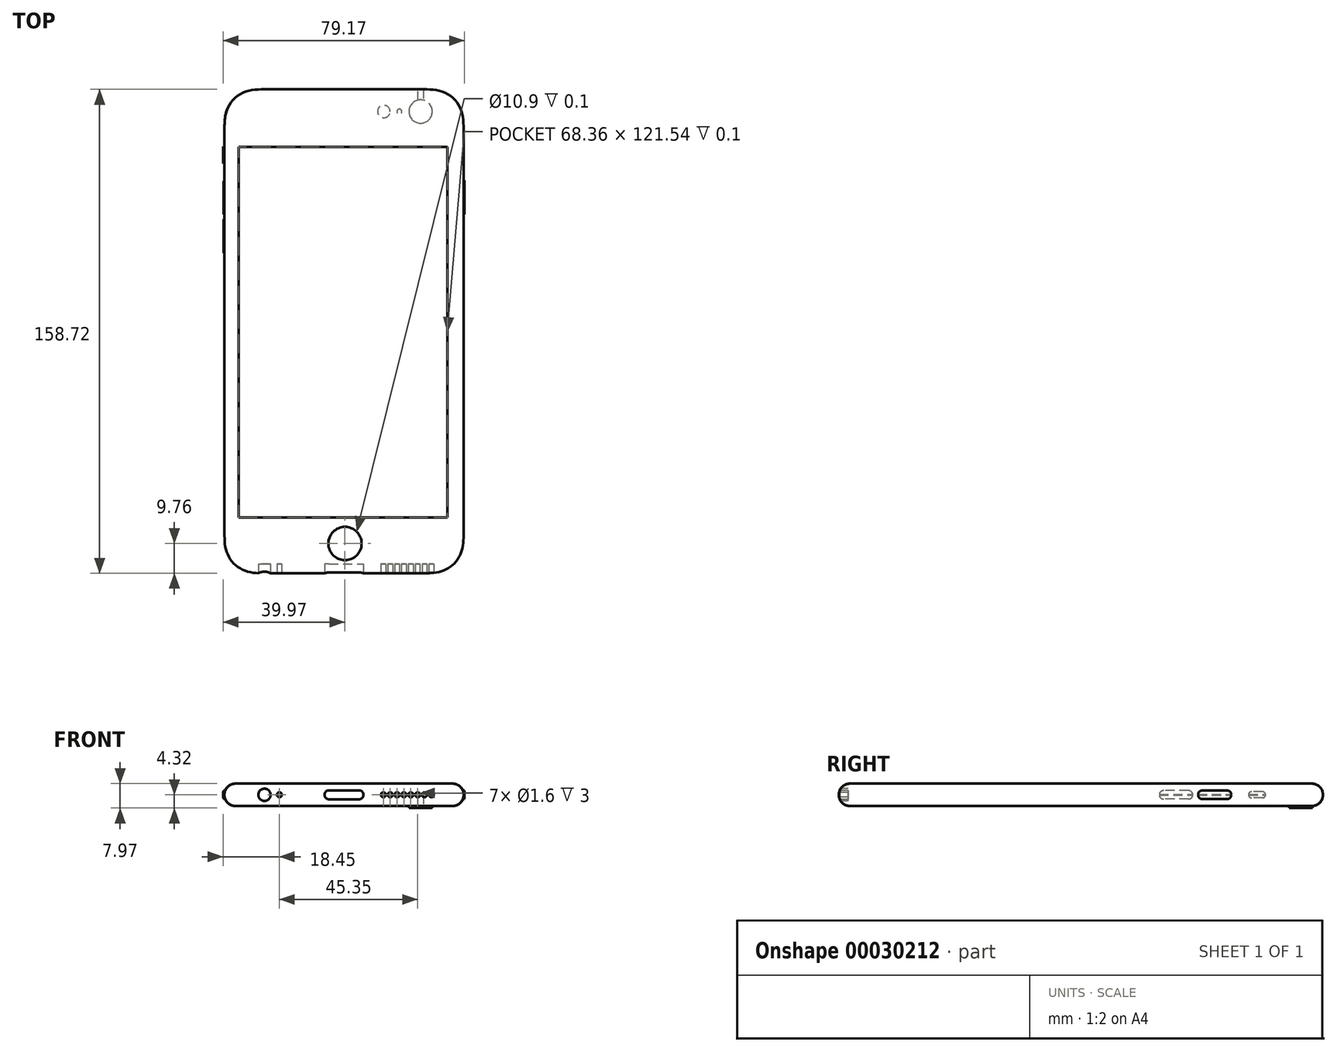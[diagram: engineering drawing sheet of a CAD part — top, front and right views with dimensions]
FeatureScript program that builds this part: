
annotation { "Feature Type Name" : "Feature", "Feature Type Description" : "" }
export const myFeature = defineFeature(function(context is Context, id is Id, definition is map)
    precondition{}
    {
        {
            var Q0;
            Q0=qCreatedBy(makeId("Top.planeOp"),FACE);
            var sketch = newSketch(context, id + "F0", { "sketchPlane" : qUnion([Q0])});
            skLineSegment(sketch, "E0.rect.bottom", {"start": v(25.09, -79.36) * mm, "end": v(-25.09, -79.36) * mm});
            skLineSegment(sketch, "E0.rect.top", {"start": v(25.09, 79.36) * mm, "end": v(-25.09, 79.36) * mm});
            skLineSegment(sketch, "E0.rect.left", {"start": v(39.22, -65.23) * mm, "end": v(39.22, 65.23) * mm});
            skLineSegment(sketch, "E0.rect.right", {"start": v(-39.22, -65.23) * mm, "end": v(-39.22, 65.23) * mm});
            skPoint(sketch, "E0.rect.middle", {"position": v(0, 0) * mm});
            skCircle(sketch, "E1", {"center": v(25.12, 72.09) * mm, "radius": 3.83 * mm});
            skCircle(sketch, "E2", {"center": v(18.16, 72.09) * mm, "radius": 0.8 * mm});
            skCircle(sketch, "E3", {"center": v(13.06, 72.09) * mm, "radius": 2.06 * mm});
            skLineSegment(sketch, "E4", {"start": v(-39.22, 72.1) * mm, "end": v(39.22, 72.1) * mm, "construction": true});
            skPoint(sketch, "E5.visualSharp", {"position": v(-39.22, 79.36) * mm});
            skFitSpline(sketch, "E6", {"points": [v(-25.09, 79.36) * mm, v(-29.02, 79.25) * mm, v(-32.83, 78.38) * mm, v(-36.09, 76.23) * mm, v(-38.24, 72.97) * mm, v(-39.1, 69.16) * mm, v(-39.22, 65.23) * mm], "startDerivative": vector(-8.98, 0) * mm, "endDerivative": vector(0, -8.98) * mm});
            skLineSegment(sketch, "E7", {"start": v(-25.09, 79.36) * mm, "end": v(-39.22, 79.36) * mm, "construction": true});
            skLineSegment(sketch, "E8", {"start": v(-39.22, 79.36) * mm, "end": v(-39.22, 65.23) * mm, "construction": true});
            skLineSegment(sketch, "E9", {"start": v(0, 79.36) * mm, "end": v(0, -79.36) * mm, "construction": true});
            skLineSegment(sketch, "E10", {"start": v(-39.22, 0) * mm, "end": v(39.22, 0) * mm, "construction": true});
            skFitSpline(sketch, "E11.MirrorCS", {"points": [v(25.09, 79.36) * mm, v(29.02, 79.25) * mm, v(32.83, 78.38) * mm, v(36.09, 76.23) * mm, v(38.24, 72.97) * mm, v(39.1, 69.16) * mm, v(39.22, 65.23) * mm], "startDerivative": vector(8.98, 0) * mm, "endDerivative": vector(0, -8.98) * mm});
            skFitSpline(sketch, "E12.MirrorCS", {"points": [v(-25.09, -79.36) * mm, v(-29.02, -79.25) * mm, v(-32.83, -78.38) * mm, v(-36.09, -76.23) * mm, v(-38.24, -72.97) * mm, v(-39.1, -69.16) * mm, v(-39.22, -65.23) * mm], "startDerivative": vector(-8.98, 0) * mm, "endDerivative": vector(0, 8.98) * mm});
            skFitSpline(sketch, "E13.MirrorCS", {"points": [v(25.09, -79.36) * mm, v(29.02, -79.25) * mm, v(32.83, -78.38) * mm, v(36.09, -76.23) * mm, v(38.24, -72.97) * mm, v(39.1, -69.16) * mm, v(39.22, -65.23) * mm], "startDerivative": vector(8.98, 0) * mm, "endDerivative": vector(0, 8.98) * mm});
            skCircle(sketch, "E14", {"center": v(0, 37.36) * mm, "radius": 11 * mm, "construction": true});
            skSolve(sketch);
        }
        {
            var Q0;
            Q0=makeQuery(id+"F0.imprint","IMPRINT",FACE,{"disambiguationData":[TD([[makeQuery(id+"F0.imprint","IMPRINT",EDGE,{"derivedFrom":sQuery(id+"F0.wireOp",EDGE,"E0.rect.bottom")}),-1.0]])]});
            var Q1;
            Q1=makeQuery(id+"F0.imprint","IMPRINT",FACE,{"disambiguationData":[TD([[makeQuery(id+"F0.imprint","IMPRINT",EDGE,{"derivedFrom":sQuery(id+"F0.wireOp",EDGE,"E1")}),1.0]])]});
            var Q2;
            Q2=makeQuery(id+"F0.imprint","IMPRINT",FACE,{"disambiguationData":[TD([[makeQuery(id+"F0.imprint","IMPRINT",EDGE,{"derivedFrom":sQuery(id+"F0.wireOp",EDGE,"E2")}),1.0]])]});
            var Q3;
            Q3=makeQuery(id+"F0.imprint","IMPRINT",FACE,{"disambiguationData":[TD([[makeQuery(id+"F0.imprint","IMPRINT",EDGE,{"derivedFrom":sQuery(id+"F0.wireOp",EDGE,"E3")}),1.0]])]});
            extrude(context, id + "F1", {"entities" : qUnion([Q0, Q1, Q2, Q3]), "depth" : 7.3 * mm});
        }
        {
            var Q0;
            Q0=makeQuery(id+"F0.imprint","IMPRINT",FACE,{"disambiguationData":[TD([[makeQuery(id+"F0.imprint","IMPRINT",EDGE,{"derivedFrom":sQuery(id+"F0.wireOp",EDGE,"E1")}),1.0]])]});
            extrude(context, id + "F2", {"entities" : qUnion([Q0]), "operationType" : NewBodyOperationType.ADD, "oppositeDirection" : true, "depth" : 0.67 * mm});
        }
        {
            var Q0;
            Q0=makeQuery(id+"F0.imprint","IMPRINT",FACE,{"disambiguationData":[TD([[makeQuery(id+"F0.imprint","IMPRINT",EDGE,{"derivedFrom":sQuery(id+"F0.wireOp",EDGE,"E3")}),1.0]])]});
            var Q1;
            Q1=makeQuery(id+"F0.imprint","IMPRINT",FACE,{"disambiguationData":[TD([[makeQuery(id+"F0.imprint","IMPRINT",EDGE,{"derivedFrom":sQuery(id+"F0.wireOp",EDGE,"E2")}),1.0]])]});
            extrude(context, id + "F3", {"entities" : qUnion([Q0, Q1]), "operationType" : NewBodyOperationType.REMOVE, "depth" : 0.1 * mm});
        }
        {
            var Q0;
            Q0=makeQuery(id+"F1.opExtrude","CAP_FACE",FACE,{"disambiguationData":[OSD([sQuery(id+"F0.wireOp",EDGE,"E0.rect.bottom"),sQuery(id+"F0.wireOp",EDGE,"E0.rect.top"),sQuery(id+"F0.wireOp",EDGE,"E0.rect.left"),sQuery(id+"F0.wireOp",EDGE,"E0.rect.right"),sQuery(id+"F0.wireOp",EDGE,"d7852d5b-fe0f-4a90-bdf2-04cff158e1f8.filletArc"),sQuery(id+"F0.wireOp",EDGE,"E5.filletArc"),sQuery(id+"F0.wireOp",EDGE,"7c06d2e9-cdf6-4879-9dee-aab3bc7c6033.filletArc"),sQuery(id+"F0.wireOp",EDGE,"93b3bdb9-dbb8-49f8-8f1e-002f612095da.filletArc")])],"isStart":false});
            var sketch = newSketch(context, id + "F4", { "sketchPlane" : qUnion([Q0])});
            skCircle(sketch, "E15", {"center": v(0.32, -69.6) * mm, "radius": 5.45 * mm});
            skLineSegment(sketch, "E16.bottom", {"start": v(-34.51, 60.44) * mm, "end": v(33.85, 60.44) * mm});
            skLineSegment(sketch, "E16.top", {"start": v(-34.5, -61.1) * mm, "end": v(33.85, -61.1) * mm});
            skLineSegment(sketch, "E16.left", {"start": v(-34.51, 60.44) * mm, "end": v(-34.5, -61.1) * mm});
            skLineSegment(sketch, "E16.right", {"start": v(33.85, 60.44) * mm, "end": v(33.85, -61.1) * mm});
            skSolve(sketch);
        }
        {
            var Q0;
            Q0=makeQuery(id+"F4.imprint","IMPRINT",FACE,{"disambiguationData":[TD([[makeQuery(id+"F4.imprint","IMPRINT",EDGE,{"derivedFrom":sQuery(id+"F4.wireOp",EDGE,"E15")}),1.0]])]});
            extrude(context, id + "F5", {"entities" : qUnion([Q0]), "operationType" : NewBodyOperationType.REMOVE, "oppositeDirection" : true, "depth" : 0.1 * mm});
        }
        {
            var Q0;
            Q0=makeQuery(id+"F4.imprint","IMPRINT",FACE,{"disambiguationData":[TD([[makeQuery(id+"F4.imprint","IMPRINT",EDGE,{"derivedFrom":sQuery(id+"F4.wireOp",EDGE,"E16.bottom")}),-1.0]])]});
            extrude(context, id + "F6", {"entities" : qUnion([Q0]), "operationType" : NewBodyOperationType.REMOVE, "oppositeDirection" : true, "depth" : 0.1 * mm});
        }
        {
            var Q0;
            Q0=makeQuery(id+"F1.opExtrude","SWEPT_FACE",FACE,{"disambiguationData":[OSD([sQuery(id+"F0.wireOp",EDGE,"E0.rect.bottom")])]});
            var sketch = newSketch(context, id + "F7", { "sketchPlane" : qUnion([Q0])});
            skLineSegment(sketch, "E17.0", {"start": v(25.09, 7.3) * mm, "end": v(-25.09, 7.3) * mm, "construction": true});
            skLineSegment(sketch, "E17.1", {"start": v(25.09, 0) * mm, "end": v(-25.09, 0) * mm, "construction": true});
            skLineSegment(sketch, "E17.2", {"start": v(39.22, 7.3) * mm, "end": v(39.22, 0) * mm, "construction": true});
            skLineSegment(sketch, "E17.3", {"start": v(-39.22, 7.3) * mm, "end": v(-39.22, 0) * mm, "construction": true});
            skFitSpline(sketch, "E17.4", {"points": [v(-24.74, 7.3) * mm, v(-29.45, 7.3) * mm, v(-34.16, 7.3) * mm, v(-38.87, 7.3) * mm], "construction": true});
            skFitSpline(sketch, "E17.5", {"points": [v(-24.74, 0) * mm, v(-29.45, 0) * mm, v(-34.16, 0) * mm, v(-38.87, 0) * mm], "construction": true});
            skFitSpline(sketch, "E17.6", {"points": [v(24.74, 0) * mm, v(29.45, 0) * mm, v(34.16, 0) * mm, v(38.87, 0) * mm], "construction": true});
            skFitSpline(sketch, "E17.7", {"points": [v(24.74, 7.3) * mm, v(29.45, 7.3) * mm, v(34.16, 7.3) * mm, v(38.87, 7.3) * mm], "construction": true});
            skLineSegment(sketch, "E18", {"start": v(0, 7.3) * mm, "end": v(0, 0) * mm, "construction": true});
            skLineSegment(sketch, "E19", {"start": v(-39.22, 3.65) * mm, "end": v(-6.4, 3.65) * mm, "construction": true});
            skLineSegment(sketch, "E20", {"start": v(-4.92, 5.12) * mm, "end": v(4.92, 5.12) * mm});
            skLineSegment(sketch, "E21", {"start": v(-4.92, 2.17) * mm, "end": v(4.92, 2.17) * mm});
            skLineSegment(sketch, "E22", {"start": v(-6.4, 3.65) * mm, "end": v(39.22, 3.65) * mm, "construction": true});
            skArc(sketch, "E23", {"start": v(-4.92, 5.13) * mm, "mid": v(-6.4, 3.65) * mm, "end": v(-4.92, 2.17) * mm});
            skArc(sketch, "E24", {"start": v(-4.92, 2.17) * mm, "mid": v(-3.44, 3.65) * mm, "end": v(-4.92, 5.13) * mm, "construction": true});
            skArc(sketch, "E25", {"start": v(4.92, 5.13) * mm, "mid": v(5.96, 4.7) * mm, "end": v(6.4, 3.65) * mm});
            skArc(sketch, "E26", {"start": v(4.92, 2.17) * mm, "mid": v(3.44, 3.65) * mm, "end": v(4.92, 5.13) * mm, "construction": true});
            skArc(sketch, "E27", {"start": v(6.4, 3.65) * mm, "mid": v(5.96, 2.6) * mm, "end": v(4.92, 2.17) * mm});
            skCircle(sketch, "E28", {"center": v(-26.09, 3.65) * mm, "radius": 2 * mm});
            skCircle(sketch, "E29", {"center": v(-21.2, 3.65) * mm, "radius": 0.8 * mm});
            skCircle(sketch, "E30", {"center": v(12.9, 3.65) * mm, "radius": 0.8 * mm});
            skCircle(sketch, "E31.1.0.0", {"center": v(15.15, 3.65) * mm, "radius": 0.8 * mm});
            skCircle(sketch, "E31.2.0.0", {"center": v(17.4, 3.65) * mm, "radius": 0.8 * mm});
            skCircle(sketch, "E31.3.0.0", {"center": v(19.65, 3.65) * mm, "radius": 0.8 * mm});
            skCircle(sketch, "E31.4.0.0", {"center": v(21.9, 3.65) * mm, "radius": 0.8 * mm});
            skCircle(sketch, "E31.5.0.0", {"center": v(24.15, 3.65) * mm, "radius": 0.8 * mm});
            skCircle(sketch, "E31.6.0.0", {"center": v(26.4, 3.65) * mm, "radius": 0.8 * mm});
            skCircle(sketch, "E31.7.0.0", {"center": v(28.65, 3.65) * mm, "radius": 0.8 * mm});
            skLineSegment(sketch, "E31.direction1", {"start": v(12.9, 3.65) * mm, "end": v(15.15, 3.65) * mm, "construction": true});
            skPoint(sketch, "E32", {"position": v(12.1, 3.65) * mm});
            skPoint(sketch, "E33", {"position": v(29.45, 3.65) * mm});
            skLineSegment(sketch, "E34.0", {"start": v(-25.09, 7.3) * mm, "end": v(-25.09, 0) * mm, "construction": true});
            skLineSegment(sketch, "E34.1", {"start": v(25.09, 7.3) * mm, "end": v(25.09, 0) * mm, "construction": true});
            skSolve(sketch);
        }
        {
            var Q0;
            Q0=makeQuery(id+"F1.opExtrude","SWEPT_FACE",FACE,{"disambiguationData":[OSD([sQuery(id+"F0.wireOp",EDGE,"E0.rect.left")])]});
            var sketch = newSketch(context, id + "F8", { "sketchPlane" : qUnion([Q0])});
            skLineSegment(sketch, "E35", {"start": v(-65.23, 2.25) * mm, "end": v(65.23, 2.25) * mm, "construction": true});
            skLineSegment(sketch, "E36", {"start": v(8.97, 4.69) * mm, "end": v(22.34, 4.7) * mm});
            skLineSegment(sketch, "E37", {"start": v(8.97, 2.25) * mm, "end": v(22.34, 2.25) * mm});
            skPoint(sketch, "E38", {"position": v(7.75, 3.47) * mm});
            skPoint(sketch, "E39", {"position": v(23.56, 3.47) * mm});
            skLineSegment(sketch, "E40", {"start": v(39.81, 2.25) * mm, "end": v(47.95, 2.25) * mm});
            skLineSegment(sketch, "E41", {"start": v(39.81, 5.05) * mm, "end": v(39.81, 5.05) * mm});
            skLineSegment(sketch, "E42", {"start": v(39.81, 3.65) * mm, "end": v(47.95, 3.65) * mm, "construction": true});
            skLineSegment(sketch, "E43", {"start": v(39.81, 5.05) * mm, "end": v(47.95, 5.05) * mm});
            skArc(sketch, "E44", {"start": v(47.95, 5.05) * mm, "mid": v(46.55, 3.65) * mm, "end": v(47.95, 2.25) * mm, "construction": true});
            skArc(sketch, "E45", {"start": v(47.95, 2.25) * mm, "mid": v(49.35, 3.65) * mm, "end": v(47.95, 5.05) * mm});
            skArc(sketch, "E46", {"start": v(39.81, 2.25) * mm, "mid": v(41.21, 3.65) * mm, "end": v(39.81, 5.05) * mm, "construction": true});
            skArc(sketch, "E47", {"start": v(39.81, 5.05) * mm, "mid": v(38.41, 3.65) * mm, "end": v(39.81, 2.25) * mm});
            skPoint(sketch, "E48", {"position": v(43.88, 3.65) * mm});
            skPoint(sketch, "E49", {"position": v(38.4, 3.65) * mm});
            skArc(sketch, "E50", {"start": v(8.97, 4.7) * mm, "mid": v(7.75, 3.47) * mm, "end": v(8.97, 2.25) * mm});
            skArc(sketch, "E51", {"start": v(8.97, 2.25) * mm, "mid": v(10.2, 3.47) * mm, "end": v(8.97, 4.7) * mm, "construction": true});
            skArc(sketch, "E52", {"start": v(22.34, 4.7) * mm, "mid": v(21.12, 3.47) * mm, "end": v(22.34, 2.25) * mm, "construction": true});
            skArc(sketch, "E53", {"start": v(22.34, 2.25) * mm, "mid": v(23.56, 3.47) * mm, "end": v(22.34, 4.7) * mm});
            skSolve(sketch);
        }
        {
            var Q0;
            Q0=makeQuery(id+"F1.opExtrude","SWEPT_FACE",FACE,{"disambiguationData":[OSD([sQuery(id+"F0.wireOp",EDGE,"E0.rect.right")])]});
            var sketch = newSketch(context, id + "F9", { "sketchPlane" : qUnion([Q0])});
            skLineSegment(sketch, "E54", {"start": v(-65.23, 3.63) * mm, "end": v(65.23, 3.63) * mm, "construction": true});
            skLineSegment(sketch, "E55", {"start": v(-60.58, 3.65) * mm, "end": v(-54.97, 3.65) * mm, "construction": true});
            skLineSegment(sketch, "E56", {"start": v(-59.6, 2.66) * mm, "end": v(-55.95, 2.66) * mm});
            skLineSegment(sketch, "E57", {"start": v(-59.6, 4.63) * mm, "end": v(-55.95, 4.63) * mm});
            skArc(sketch, "E58", {"start": v(-59.6, 2.66) * mm, "mid": v(-58.61, 3.64) * mm, "end": v(-59.6, 4.63) * mm, "construction": true});
            skArc(sketch, "E59", {"start": v(-59.6, 4.63) * mm, "mid": v(-60.58, 3.64) * mm, "end": v(-59.6, 2.66) * mm});
            skArc(sketch, "E60", {"start": v(-55.95, 2.66) * mm, "mid": v(-54.97, 3.65) * mm, "end": v(-55.95, 4.63) * mm});
            skArc(sketch, "E61", {"start": v(-55.95, 4.63) * mm, "mid": v(-56.94, 3.65) * mm, "end": v(-55.95, 2.66) * mm, "construction": true});
            skPoint(sketch, "E62.first.point", {"position": v(-49.28, 3.63) * mm});
            skPoint(sketch, "E62.second.point", {"position": v(-47.88, 2.23) * mm});
            skPoint(sketch, "E62.third.point", {"position": v(-47.88, 5.03) * mm});
            skPoint(sketch, "E63.first.point", {"position": v(-41.14, 3.63) * mm});
            skPoint(sketch, "E63.second.point", {"position": v(-39.74, 2.23) * mm});
            skPoint(sketch, "E63.third.point", {"position": v(-39.74, 5.03) * mm});
            skLineSegment(sketch, "E64", {"start": v(-47.88, 2.23) * mm, "end": v(-39.74, 2.23) * mm});
            skLineSegment(sketch, "E65", {"start": v(-47.88, 5.03) * mm, "end": v(-39.74, 5.03) * mm});
            skArc(sketch, "E66", {"start": v(-47.88, 5.03) * mm, "mid": v(-49.28, 3.63) * mm, "end": v(-47.88, 2.23) * mm});
            skArc(sketch, "E67", {"start": v(-47.88, 2.23) * mm, "mid": v(-46.48, 3.63) * mm, "end": v(-47.88, 5.03) * mm, "construction": true});
            skArc(sketch, "E68", {"start": v(-39.74, 2.23) * mm, "mid": v(-38.34, 3.63) * mm, "end": v(-39.74, 5.03) * mm});
            skArc(sketch, "E69", {"start": v(-39.74, 5.03) * mm, "mid": v(-41.14, 3.63) * mm, "end": v(-39.74, 2.23) * mm, "construction": true});
            skLineSegment(sketch, "E70", {"start": v(-47.88, 3.63) * mm, "end": v(-39.74, 3.63) * mm, "construction": true});
            skPoint(sketch, "E71", {"position": v(-43.81, 3.63) * mm});
            skLineSegment(sketch, "E72", {"start": v(-35.27, 2.23) * mm, "end": v(-27.13, 2.23) * mm});
            skLineSegment(sketch, "E73", {"start": v(-35.27, 5.03) * mm, "end": v(-27.13, 5.03) * mm});
            skPoint(sketch, "E74.third.point", {"position": v(-36.67, 3.63) * mm});
            skPoint(sketch, "E75.third.point", {"position": v(-25.73, 3.63) * mm});
            skLineSegment(sketch, "E76", {"start": v(-27.13, 3.63) * mm, "end": v(-35.27, 3.63) * mm, "construction": true});
            skPoint(sketch, "E77", {"position": v(-31.2, 3.63) * mm});
            skArc(sketch, "E78", {"start": v(-35.27, 2.23) * mm, "mid": v(-33.87, 3.63) * mm, "end": v(-35.27, 5.03) * mm, "construction": true});
            skArc(sketch, "E79", {"start": v(-35.27, 5.03) * mm, "mid": v(-36.67, 3.63) * mm, "end": v(-35.27, 2.23) * mm});
            skArc(sketch, "E80", {"start": v(-27.13, 5.03) * mm, "mid": v(-28.53, 3.63) * mm, "end": v(-27.13, 2.23) * mm, "construction": true});
            skArc(sketch, "E81", {"start": v(-27.13, 2.23) * mm, "mid": v(-25.73, 3.63) * mm, "end": v(-27.13, 5.03) * mm});
            skSolve(sketch);
        }
        {
            var Q0;
            Q0=makeQuery(id+"F1.opExtrude","CAP_EDGE",EDGE,{"disambiguationData":[OSD([sQuery(id+"F0.wireOp",EDGE,"E0.rect.top")])],"isStart":false});
            var Q1;
            Q1=makeQuery(id+"F1.opExtrude","CAP_EDGE",EDGE,{"disambiguationData":[OSD([sQuery(id+"F0.wireOp",EDGE,"E0.rect.top")])],"isStart":true});
            fillet(context, id + "F10", {"entities" : qUnion([Q0, Q1]), "radius" : (7.1 / 2) * mm, "tangentPropagation" : true, "allowEdgeOverflow" : false});
        }
        {
            var Q0;
            {var subQ0=makeQuery(id+"F1.opExtrude","SWEPT_EDGE",EDGE,{"disambiguationData":[OSD([sQuery(id+"F0.wireOp",EDGE,"E0.rect.bottom"),sQuery(id+"F0.wireOp",EDGE,"E12.MirrorCS")])]});var subQ1=sQuery(id+"F7.wireOp",EDGE,"E28");var subQ3=makeQuery(id+"F7.imprint","INTERSECT",VERTEX,{"disambiguationData":[OD(0.0)],"derivedFrom":[subQ0,subQ1]});Q0=makeQuery(id+"F7.imprint","IMPRINT",FACE,{"disambiguationData":[TD([[makeQuery(id+"F7.imprint","IMPRINT",EDGE,{"disambiguationData":[TD([[subQ3,-1.0]])],"derivedFrom":subQ1}),1.0]])]});}
            var Q1;
            Q1=makeQuery(id+"F7.imprint","IMPRINT",FACE,{"disambiguationData":[TD([[makeQuery(id+"F7.imprint","IMPRINT",EDGE,{"derivedFrom":sQuery(id+"F7.wireOp",EDGE,"E29")}),1.0]])]});
            var Q2;
            Q2=makeQuery(id+"F7.imprint","IMPRINT",FACE,{"disambiguationData":[TD([[makeQuery(id+"F7.imprint","IMPRINT",EDGE,{"derivedFrom":sQuery(id+"F7.wireOp",EDGE,"E20")}),-1.0]])]});
            var Q3;
            Q3=makeQuery(id+"F7.imprint","IMPRINT",FACE,{"disambiguationData":[TD([[makeQuery(id+"F7.imprint","IMPRINT",EDGE,{"derivedFrom":sQuery(id+"F7.wireOp",EDGE,"E30")}),1.0]])]});
            var Q4;
            Q4=makeQuery(id+"F7.imprint","IMPRINT",FACE,{"disambiguationData":[TD([[makeQuery(id+"F7.imprint","IMPRINT",EDGE,{"derivedFrom":sQuery(id+"F7.wireOp",EDGE,"E31.1.0.0")}),1.0]])]});
            var Q5;
            Q5=makeQuery(id+"F7.imprint","IMPRINT",FACE,{"disambiguationData":[TD([[makeQuery(id+"F7.imprint","IMPRINT",EDGE,{"derivedFrom":sQuery(id+"F7.wireOp",EDGE,"E31.2.0.0")}),1.0]])]});
            var Q6;
            Q6=makeQuery(id+"F7.imprint","IMPRINT",FACE,{"disambiguationData":[TD([[makeQuery(id+"F7.imprint","IMPRINT",EDGE,{"derivedFrom":sQuery(id+"F7.wireOp",EDGE,"E31.3.0.0")}),1.0]])]});
            var Q7;
            Q7=makeQuery(id+"F7.imprint","IMPRINT",FACE,{"disambiguationData":[TD([[makeQuery(id+"F7.imprint","IMPRINT",EDGE,{"derivedFrom":sQuery(id+"F7.wireOp",EDGE,"E31.4.0.0")}),1.0]])]});
            var Q8;
            Q8=makeQuery(id+"F7.imprint","IMPRINT",FACE,{"disambiguationData":[TD([[makeQuery(id+"F7.imprint","IMPRINT",EDGE,{"derivedFrom":sQuery(id+"F7.wireOp",EDGE,"E31.5.0.0")}),1.0]])]});
            var Q9;
            Q9=makeQuery(id+"F7.imprint","IMPRINT",FACE,{"disambiguationData":[TD([[makeQuery(id+"F7.imprint","IMPRINT",EDGE,{"derivedFrom":sQuery(id+"F7.wireOp",EDGE,"E31.6.0.0")}),1.0]])]});
            var Q10;
            Q10=makeQuery(id+"F7.imprint","IMPRINT",FACE,{"disambiguationData":[TD([[makeQuery(id+"F7.imprint","IMPRINT",EDGE,{"derivedFrom":sQuery(id+"F7.wireOp",EDGE,"E31.7.0.0")}),1.0]])]});
            var Q11;
            {var subQ0=makeQuery(id+"F1.opExtrude","SWEPT_EDGE",EDGE,{"disambiguationData":[OSD([sQuery(id+"F0.wireOp",EDGE,"E0.rect.bottom"),sQuery(id+"F0.wireOp",EDGE,"E12.MirrorCS")])]});var subQ1=sQuery(id+"F7.wireOp",EDGE,"E28");var subQ3=makeQuery(id+"F7.imprint","INTERSECT",VERTEX,{"disambiguationData":[OD(0.0)],"derivedFrom":[subQ0,subQ1]});Q11=makeQuery(id+"F7.imprint","IMPRINT",FACE,{"disambiguationData":[TD([[makeQuery(id+"F7.imprint","IMPRINT",EDGE,{"disambiguationData":[TD([[subQ3,1.0]])],"derivedFrom":subQ1}),1.0]])]});}
            extrude(context, id + "F11", {"entities" : qUnion([Q0, Q1, Q2, Q3, Q4, Q5, Q6, Q7, Q8, Q9, Q10, Q11]), "oppositeDirection" : true, "depth" : 3 * mm, "hasSecondDirection" : true, "secondDirectionOppositeDirection" : false, "secondDirectionDepth" : 1 * mm});
        }
        {
            var Q0;
            Q0=makeQuery(id+"F11.opExtrude","SWEPT_BODY",BODY,{"disambiguationData":[OSD([sQuery(id+"F7.wireOp",EDGE,"E28")])]});
            var Q1;
            Q1=makeQuery(id+"F11.opExtrude","SWEPT_BODY",BODY,{"disambiguationData":[OSD([sQuery(id+"F7.wireOp",EDGE,"E29")])]});
            var Q2;
            Q2=makeQuery(id+"F11.opExtrude","SWEPT_BODY",BODY,{"disambiguationData":[OSD([sQuery(id+"F7.wireOp",EDGE,"E30")])]});
            var Q3;
            Q3=makeQuery(id+"F11.opExtrude","SWEPT_BODY",BODY,{"disambiguationData":[OSD([sQuery(id+"F7.wireOp",EDGE,"E31.1.0.0")])]});
            var Q4;
            Q4=makeQuery(id+"F11.opExtrude","SWEPT_BODY",BODY,{"disambiguationData":[OSD([sQuery(id+"F7.wireOp",EDGE,"E31.2.0.0")])]});
            var Q5;
            Q5=makeQuery(id+"F11.opExtrude","SWEPT_BODY",BODY,{"disambiguationData":[OSD([sQuery(id+"F7.wireOp",EDGE,"E31.3.0.0")])]});
            var Q6;
            Q6=makeQuery(id+"F11.opExtrude","SWEPT_BODY",BODY,{"disambiguationData":[OSD([sQuery(id+"F7.wireOp",EDGE,"E31.4.0.0")])]});
            var Q7;
            Q7=makeQuery(id+"F11.opExtrude","SWEPT_BODY",BODY,{"disambiguationData":[OSD([sQuery(id+"F7.wireOp",EDGE,"E31.5.0.0")])]});
            var Q8;
            Q8=makeQuery(id+"F11.opExtrude","SWEPT_BODY",BODY,{"disambiguationData":[OSD([sQuery(id+"F7.wireOp",EDGE,"E31.6.0.0")])]});
            var Q9;
            Q9=makeQuery(id+"F11.opExtrude","SWEPT_BODY",BODY,{"disambiguationData":[OSD([sQuery(id+"F7.wireOp",EDGE,"E31.7.0.0")])]});
            var Q10;
            Q10=makeQuery(id+"F11.opExtrude","SWEPT_BODY",BODY,{"disambiguationData":[OSD([sQuery(id+"F7.wireOp",EDGE,"E20"),sQuery(id+"F7.wireOp",EDGE,"E21"),sQuery(id+"F7.wireOp",EDGE,"E23"),sQuery(id+"F7.wireOp",EDGE,"E25"),sQuery(id+"F7.wireOp",EDGE,"E27")])]});
            var Q11;
            Q11=makeQuery(id+"F1.opExtrude","SWEPT_BODY",BODY,{"disambiguationData":[OSD([sQuery(id+"F0.wireOp",EDGE,"E0.rect.bottom"),sQuery(id+"F0.wireOp",EDGE,"E0.rect.top"),sQuery(id+"F0.wireOp",EDGE,"E0.rect.left"),sQuery(id+"F0.wireOp",EDGE,"E0.rect.right"),sQuery(id+"F0.wireOp",EDGE,"E6"),sQuery(id+"F0.wireOp",EDGE,"E11.MirrorCS"),sQuery(id+"F0.wireOp",EDGE,"E12.MirrorCS"),sQuery(id+"F0.wireOp",EDGE,"E13.MirrorCS")])]});
            booleanBodies(context, id + "F12", {"operationType" : BooleanOperationType.SUBTRACTION, "tools" : qUnion([Q0, Q1, Q2, Q3, Q4, Q5, Q6, Q7, Q8, Q9, Q10]), "targets" : qUnion([Q11])});
        }
        {
            var Q0;
            Q0=makeQuery(id+"F8.imprint","IMPRINT",FACE,{"disambiguationData":[TD([[makeQuery(id+"F8.imprint","IMPRINT",EDGE,{"derivedFrom":sQuery(id+"F8.wireOp",EDGE,"E40")}),1.0]])]});
            extrude(context, id + "F13", {"entities" : qUnion([Q0]), "operationType" : NewBodyOperationType.ADD, "depth" : 0.3 * mm});
        }
        {
            var Q0;
            Q0=makeQuery(id+"F9.imprint","IMPRINT",FACE,{"disambiguationData":[TD([[makeQuery(id+"F9.imprint","IMPRINT",EDGE,{"derivedFrom":sQuery(id+"F9.wireOp",EDGE,"E72")}),1.0]])]});
            var Q1;
            Q1=makeQuery(id+"F9.imprint","IMPRINT",FACE,{"disambiguationData":[TD([[makeQuery(id+"F9.imprint","IMPRINT",EDGE,{"derivedFrom":sQuery(id+"F9.wireOp",EDGE,"E64")}),1.0]])]});
            extrude(context, id + "F14", {"entities" : qUnion([Q0, Q1]), "operationType" : NewBodyOperationType.ADD, "depth" : 0.3 * mm});
        }
        {
            var Q0;
            Q0=makeQuery(id+"F9.imprint","IMPRINT",FACE,{"disambiguationData":[TD([[makeQuery(id+"F9.imprint","IMPRINT",EDGE,{"derivedFrom":sQuery(id+"F9.wireOp",EDGE,"E56")}),1.0]])]});
            extrude(context, id + "F15", {"entities" : qUnion([Q0]), "operationType" : NewBodyOperationType.ADD, "depth" : 0.43 * mm});
        }
    });
